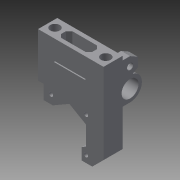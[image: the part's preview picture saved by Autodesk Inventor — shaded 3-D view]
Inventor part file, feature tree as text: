
AUTODESK INVENTOR PART (.ipt)
format: ipt  version: 2015 SP2 (Build 190223200, 223)  size: 262,656 bytes
history: native  units: mm
features: sketch x12, extrude x10, hole x3, chamfer x1
ambient origin geometry x8: Origin, YZ Plane, XZ Plane, XY Plane, X Axis, Y Axis, Z Axis, Center Point
bodies: Solid1 (feature_tree)
feature tree (26):
  extrude  "Extrusion1"  Depth=58.0mm
  extrude  "Extrusion2"  Depth=17.0mm
  sketch  "Sketch3"  dims[d5=38.0mm d6=27.75mm]
  extrude  "Extrusion4"  Depth=38.0mm
  extrude  "Extrusion5"  Depth=19.25mm TaperAngle=0.0deg
  extrude  "Extrusion6"  Depth=3.0mm
  extrude  "Extrusion7"  Depth=15.0mm
  extrude  "Extrusion9"  Depth=8.0mm
  hole  "Hole1"  [1 undecoded]
  hole  "Hole2"  [1 undecoded]
  chamfer  "Chamfer1"  Distance=28.0mm
  hole  "Hole3"  [1 undecoded]
  extrude  "Extrusion10"  Depth=10.0mm
  extrude  "Extrusion11"  Depth=22.0mm
  extrude  "Extrusion12"  Depth=10.0mm TaperAngle=0.0deg
  sketch  "Sketch1"  dims[d0=81.5mm d1=58.0mm]
  sketch  "Sketch2"  dims[d2=35.0mm d3=0.0mm d4=17.0mm]
  sketch  "Sketch4"  dims[d7=19.25mm d8=35.0mm d9=0.0mm]
  sketch  "Sketch5"  dims[d10=17.0mm d11=3.0mm]
  sketch  "Sketch6"  dims[d12=15.0mm d13=6.5mm]
  sketch  "Sketch7"  dims[d14=3.5mm d15=8.0mm]
  sketch  "Sketch8"  dims[d19=0.0mm d20=0.0mm d21=8.0mm]
  sketch  "Sketch9"  dims[d22=35.0mm d23=0.0mm d24=12.5mm]
  sketch  "Sketch12"  dims[d25=5.0mm]
  sketch  "Sketch13"  dims[d26=8.0mm]
  sketch  "Sketch15"  dims[d27=1.0mm d28=28.0mm d29=10.0mm d30=0.0mm d31=10.0mm d32=22.0mm d33=10.0mm d34=0.0mm d39=13.75mm d40=135.0deg d41=2.75mm d43=41.5mm d44=0.0mm d45=31.0mm d46=31.0mm d47=6.485mm d48=7.66mm d49=3.6mm d50=6.0mm d51=6.2mm d52=3.5mm d53=90.0deg d54=8.0mm d55=20.594885mm d56=45.0mm d57=8.5mm d58=6.5mm d59=8.5mm d60=6.0mm d61=3.023mm d62=3.5mm d63=14.3117mm d64=37.0mm d65=0.0mm d67=10.0mm d68=2.0mm d69=45.0deg d70=5.4mm d71=6.0mm d72=3.023mm d73=3.5mm d74=14.3117mm d75=41.5mm d76=0.0mm d77=3.5mm d78=7.794mm d79=5.0mm d80=0.0mm d81=1.0mm d82=1.675mm d83=5.0mm d84=0.0mm d85=17.0mm d86=120.0deg d87=6.5mm d88=15.0mm d89=10.0mm d90=0.0mm]
note: 3 required parameter values undecoded (feature->parameter linkage not recoverable at this tier; creation-order binding heuristic only, values carry confidence <= 0.55)
